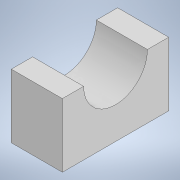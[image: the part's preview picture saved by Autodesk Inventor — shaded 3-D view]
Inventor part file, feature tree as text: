
AUTODESK INVENTOR PART (.ipt)
format: ipt  version: 2021 (Build 250183000, 183)  size: 103,936 bytes
history: native  units: in
note: dims shown in document units (in); Inventor stores cm internally (conversion verified against a paired STEP export)
features: sketch x3, extrude x2
ambient origin geometry x8: Origin, YZ Plane, XZ Plane, XY Plane, X Axis, Y Axis, Z Axis, Center Point
bodies: Solid1 (feature_tree)
feature tree (5):
  sketch  "Sketch1"  dims[d0=0.4724in d1=0.5906in]
  extrude  "Extrusion1"  Depth=0.5906in
  extrude  "Extrusion2"  Depth=0.9843in
  sketch  "Sketch2"  dims[d2=0.9843in d3=0.0in d4=0.1969in]
  sketch  "Sketch3"  dims[d5=0.1969in d6=0.2953in d7=0.9843in d8=0.0in]
